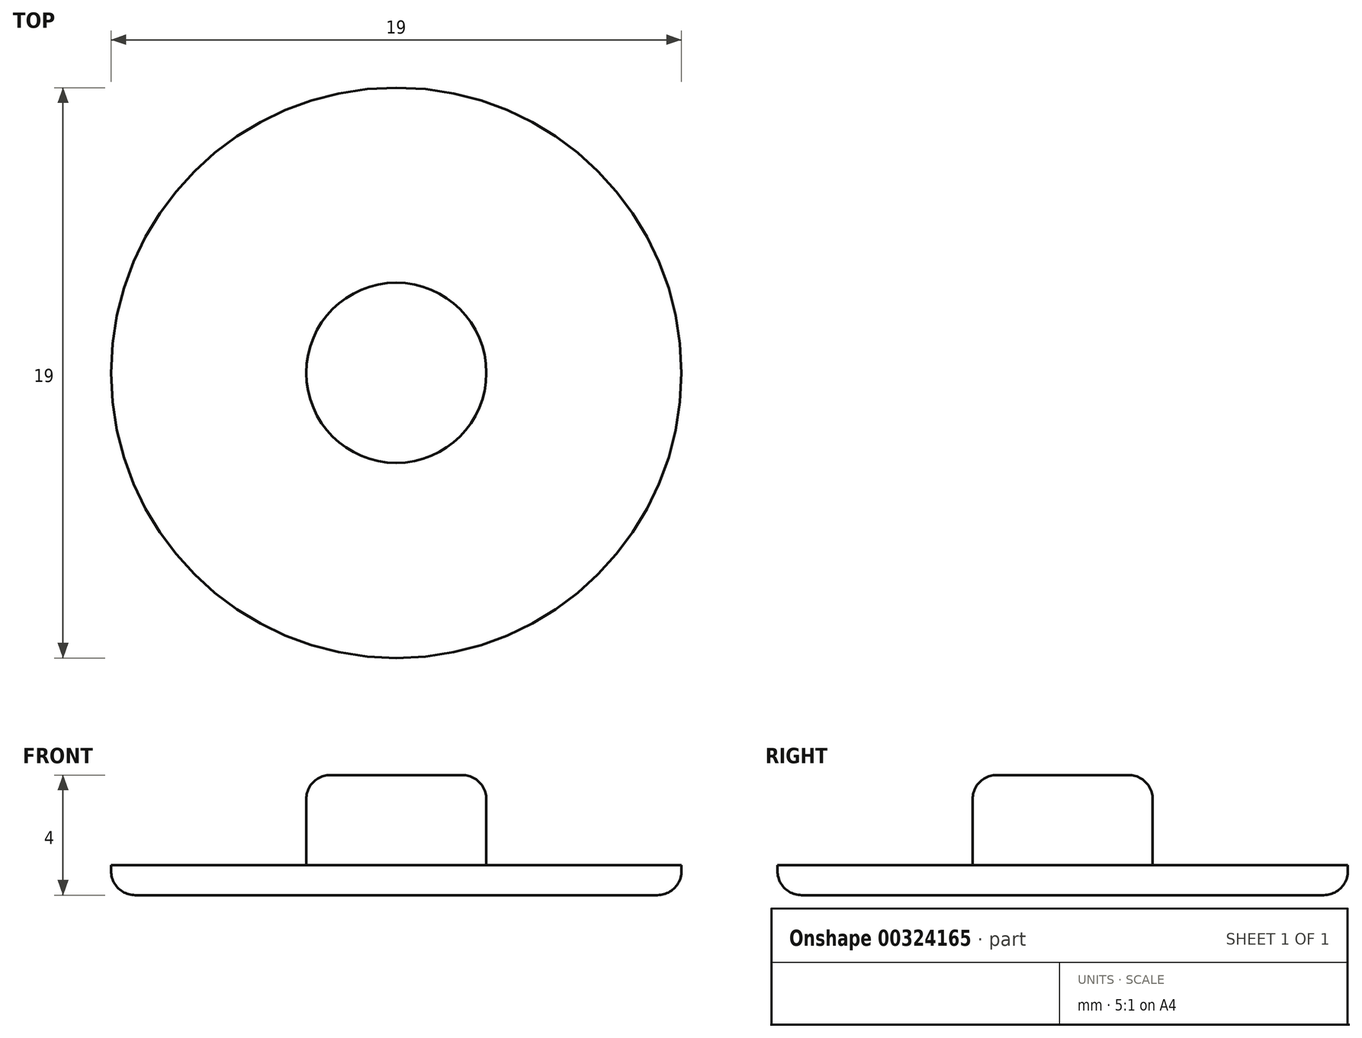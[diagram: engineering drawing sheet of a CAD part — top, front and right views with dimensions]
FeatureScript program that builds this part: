
annotation { "Feature Type Name" : "Feature", "Feature Type Description" : "" }
export const myFeature = defineFeature(function(context is Context, id is Id, definition is map)
    precondition{}
    {
        {
            var Q0;
            Q0=qCreatedBy(makeId("Top.planeOp"),FACE);
            var sketch = newSketch(context, id + "F0", { "sketchPlane" : qUnion([Q0])});
            skCircle(sketch, "E0", {"center": v(0, 0) * mm, "radius": 9.5 * mm});
            skSolve(sketch);
        }
        {
            var Q0;
            Q0=qSketchRegion(id+"F0",true);
            extrude(context, id + "F1", {"entities" : qUnion([Q0]), "depth" : 1 * mm});
        }
        {
            var Q0;
            Q0=makeQuery(id+"F1.opExtrude","CAP_FACE",FACE,{"disambiguationData":[OSD([sQuery(id+"F0.wireOp",EDGE,"E0")])],"isStart":false});
            var sketch = newSketch(context, id + "F2", { "sketchPlane" : qUnion([Q0])});
            skCircle(sketch, "E1", {"center": v(0, 0) * mm, "radius": 3 * mm});
            skSolve(sketch);
        }
        {
            var Q0;
            Q0=makeQuery(id+"F2.imprint","IMPRINT",FACE,{"disambiguationData":[TD([[makeQuery(id+"F2.imprint","IMPRINT",EDGE,{"derivedFrom":sQuery(id+"F2.wireOp",EDGE,"E1")}),1.0]])]});
            extrude(context, id + "F3", {"entities" : qUnion([Q0]), "operationType" : NewBodyOperationType.ADD, "depth" : 3 * mm});
        }
        {
            var Q0;
            Q0=makeQuery(id+"F1.opExtrude","CAP_EDGE",EDGE,{"disambiguationData":[OSD([sQuery(id+"F0.wireOp",EDGE,"E0")])],"isStart":true});
            var Q1;
            Q1=makeQuery(id+"F3.opExtrude","CAP_EDGE",EDGE,{"disambiguationData":[OSD([sQuery(id+"F2.wireOp",EDGE,"E1")])],"isStart":false});
            fillet(context, id + "F4", {"entities" : qUnion([Q0, Q1]), "radius" : .8 * mm, "tangentPropagation" : true, "allowEdgeOverflow" : false});
        }
    });
